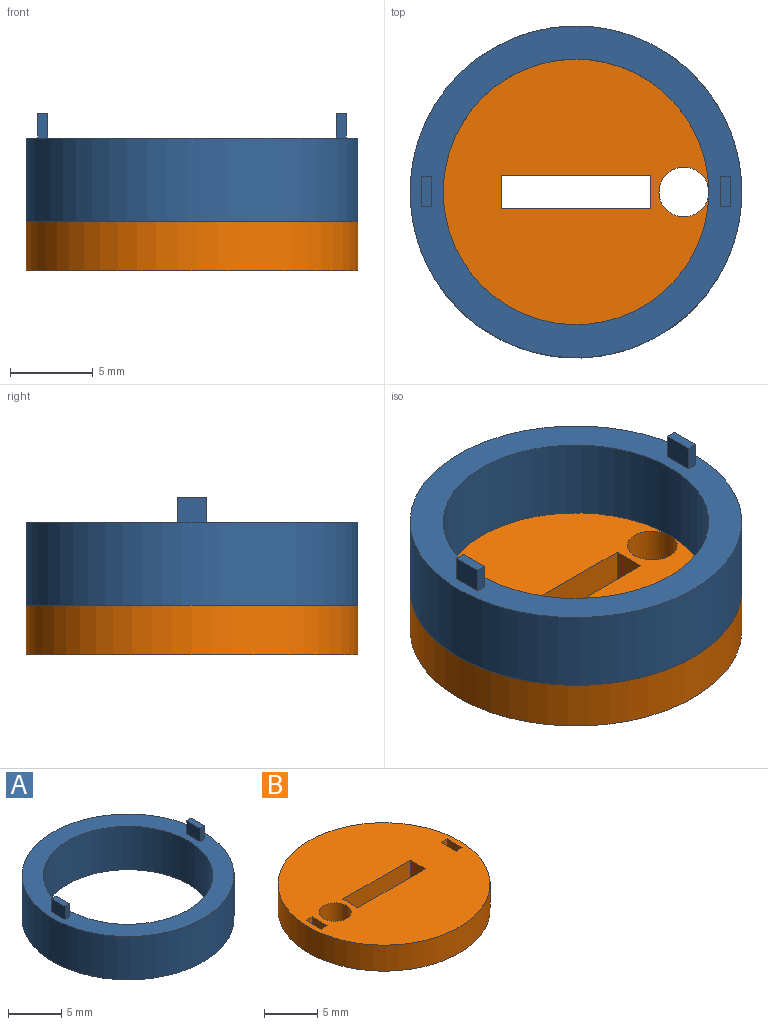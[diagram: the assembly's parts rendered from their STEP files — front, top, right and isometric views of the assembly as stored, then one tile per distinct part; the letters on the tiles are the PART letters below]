
ASSEMBLY  parts=2 mates=1
PART A: 14 faces, bbox 20x20x6.5 mm
  f0: plane 1.8x1.5mm, normal (-1,0,0), area 2.7mm2, adj f1,f3,f4,f12
  f1: plane 1.5x0.6mm, normal (0,-1,0), area 0.9mm2, adj f0,f2,f4,f12
  f2: plane 1.8x1.5mm, normal (1,0,0), area 2.7mm2, adj f1,f3,f4,f12
  f3: plane 1.5x0.6mm, normal (0,1,0), area 0.9mm2, adj f0,f2,f4,f12
  f4: plane 1.8x0.6mm, normal (0,0,1), area 1.1mm2, adj f0,f1,f2,f3
  f5: plane 1.8x1.5mm, normal (-1,0,0), area 2.7mm2, adj f6,f8,f9,f12
  f6: plane 1.5x0.6mm, normal (0,-1,0), area 0.9mm2, adj f5,f7,f9,f12
  f7: plane 1.8x1.5mm, normal (1,0,0), area 2.7mm2, adj f6,f8,f9,f12
  f8: plane 1.5x0.6mm, normal (0,1,0), area 0.9mm2, adj f5,f7,f9,f12
  f9: plane 1.8x0.6mm, normal (0,0,1), area 1.1mm2, adj f5,f6,f7,f8
  f10: cylinder r=8mm len=16mm, axis (0,0,-1), area 251.3mm2, adj f12,f13
  f11: cylinder r=10mm len=20mm, axis (0,0,-1), area 314.2mm2, adj f12,f13
  f12: plane 20x20mm, normal (0,0,1), area 110.9mm2, adj f0,f1,f2,f3,f5,f6,f7,f8
  f13: plane 20x20mm, normal (0,0,-1), area 113.1mm2, adj f10,f11
PART B: 18 faces, bbox 20x20x3 mm
  f0: plane 20x20mm, normal (0,0,-1), area 289.1mm2, adj f9,f10,f11,f12,f13,f14
  f1: plane 1.5x0.8mm, normal (0,-1,0), area 1.2mm2, adj f2,f4,f15,f17
  f2: plane 2x1.5mm, normal (1,0,0), area 3mm2, adj f1,f3,f15,f17
  f3: plane 1.5x0.8mm, normal (0,1,0), area 1.2mm2, adj f2,f4,f15,f17
  f4: plane 2x1.5mm, normal (-1,0,0), area 3mm2, adj f1,f3,f15,f17
  f5: plane 1.5x0.8mm, normal (0,-1,0), area 1.2mm2, adj f6,f8,f15,f16
  f6: plane 2x1.5mm, normal (1,0,0), area 3mm2, adj f5,f7,f15,f16
  f7: plane 1.5x0.8mm, normal (0,1,0), area 1.2mm2, adj f6,f8,f15,f16
  f8: plane 2x1.5mm, normal (-1,0,0), area 3mm2, adj f5,f7,f15,f16
  f9: plane 9x3mm, normal (0,1,0), area 27mm2, adj f0,f10,f12,f15
  f10: plane 3x2mm, normal (1,0,0), area 6mm2, adj f0,f9,f11,f15
  f11: plane 9x3mm, normal (0,-1,0), area 27mm2, adj f0,f10,f12,f15
  f12: plane 3x2mm, normal (-1,0,0), area 6mm2, adj f0,f9,f11,f15
  f13: cylinder r=1.5mm len=3mm, axis (0,0,-1), area 28.3mm2, adj f0,f15
  f14: cylinder r=10mm len=20mm, axis (0,0,-1), area 188.5mm2, adj f0,f15
  f15: plane 20x20mm, normal (0,0,1), area 285.9mm2, adj f1,f2,f3,f4,f5,f6,f7,f8
  f16: plane 2x0.8mm, normal (0,0,1), area 1.6mm2, adj f5,f6,f7,f8
  f17: plane 2x0.8mm, normal (0,0,1), area 1.6mm2, adj f1,f2,f3,f4
PLACE A t=(-0.66,9.58,2.03)mm
PLACE B rot(axis=(0,1,0),180deg) t=(-0.66,9.58,0.53)mm
MATE fastened B.f14 <-> A.f10  axis (0,0,1) through (-0.66,9.58,2.03)mm
